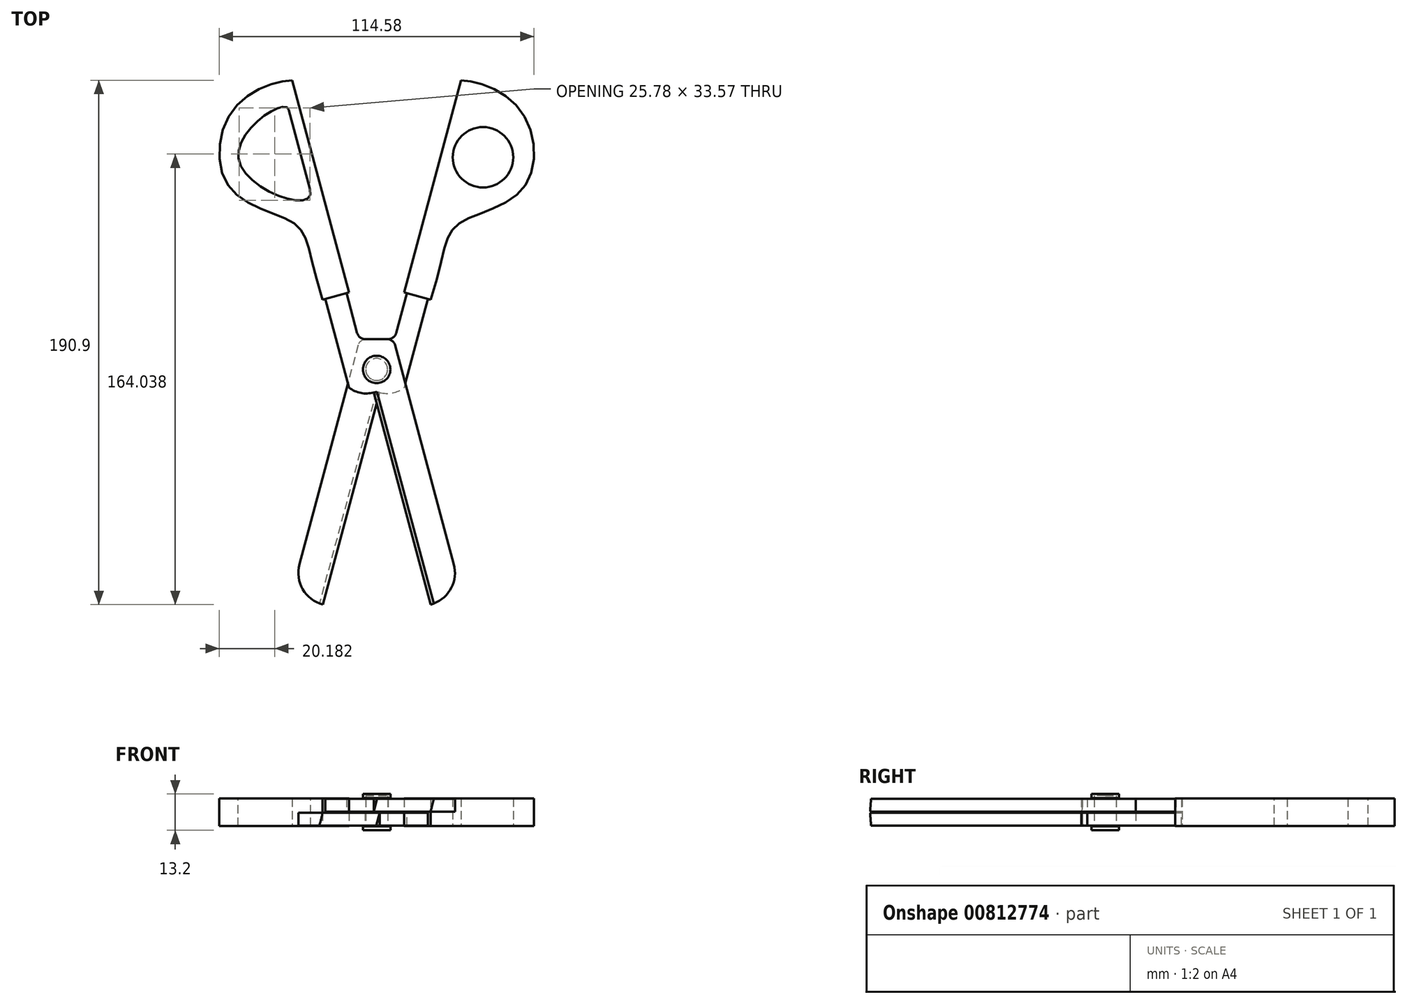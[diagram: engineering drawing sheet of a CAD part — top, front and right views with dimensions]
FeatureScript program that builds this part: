
annotation { "Feature Type Name" : "Feature", "Feature Type Description" : "" }
export const myFeature = defineFeature(function(context is Context, id is Id, definition is map)
    precondition{}
    {
        {
            var Q0;
            Q0=qCreatedBy(makeId("Top.planeOp"),FACE);
            var sketch = newSketch(context, id + "F0", { "sketchPlane" : qUnion([Q0])});
            skLineSegment(sketch, "E0", {"start": v(10, 10) * mm, "end": v(30.7, 87.27) * mm});
            skLineSegment(sketch, "E1", {"start": v(10, 10) * mm, "end": v(19.66, 7.41) * mm});
            skFitSpline(sketch, "E2", {"points": [v(19.66, 7.41) * mm, v(30.07, 35.15) * mm, v(53.27, 47.9) * mm, v(52.13, 76.77) * mm, v(30.7, 87.27) * mm], "startDerivative": vector(62.66, 194.88) * mm, "endDerivative": vector(-72.65, 2.28) * mm});
            skLineSegment(sketch, "E3.MirrorCS", {"start": v(-10, 10) * mm, "end": v(-30.7, 87.27) * mm});
            skFitSpline(sketch, "E4.MirrorCS", {"points": [v(-19.66, 7.41) * mm, v(-30.07, 35.15) * mm, v(-53.27, 47.9) * mm, v(-52.13, 76.77) * mm, v(-30.7, 87.27) * mm], "startDerivative": vector(-62.66, 194.88) * mm, "endDerivative": vector(72.65, 2.28) * mm});
            skLineSegment(sketch, "E5.MirrorCS", {"start": v(-10, 10) * mm, "end": v(-19.66, 7.41) * mm});
            skSolve(sketch);
        }
        {
            var Q0;
            Q0 = qSketchRegion(id + "F0", true);
            extrude(context, id + "F1", {"entities" : qUnion([Q0]), "endBound" : BoundingType.SYMMETRIC, "depth" : 10 * mm, "offsetDistance" : 25 * mm});
        }
        {
            var Q0;
            Q0=qCreatedBy(makeId("Top.planeOp"),FACE);
            var sketch = newSketch(context, id + "F2", { "sketchPlane" : qUnion([Q0])});
            skLineSegment(sketch, "E6", {"start": v(-31.98, 76.58) * mm, "end": v(-24.22, 47.6) * mm});
            skFitSpline(sketch, "E7", {"points": [v(-31.98, 76.58) * mm, v(-50.17, 58.1) * mm, v(-24.22, 47.6) * mm], "startDerivative": vector(-7.92, 29.54) * mm, "endDerivative": vector(-15.24, 56.87) * mm});
            skSolve(sketch);
        }
        {
            var Q0;
            Q0 = qSketchRegion(id + "F2", true);
            extrude(context, id + "F3", {"entities" : qUnion([Q0]), "operationType" : NewBodyOperationType.REMOVE, "endBound" : BoundingType.SYMMETRIC, "oppositeDirection" : true, "depth" : 40 * mm, "offsetDistance" : 25 * mm});
        }
        {
            var Q0;
            Q0=qCreatedBy(makeId("Top.planeOp"),FACE);
            var sketch = newSketch(context, id + "F4", { "sketchPlane" : qUnion([Q0])});
            skCircle(sketch, "E8", {"center": v(38.72, 59.24) * mm, "radius": 11 * mm});
            skSolve(sketch);
        }
        {
            var Q0;
            Q0 = qSketchRegion(id + "F4", true);
            extrude(context, id + "F5", {"entities" : qUnion([Q0]), "operationType" : NewBodyOperationType.REMOVE, "endBound" : BoundingType.SYMMETRIC, "depth" : 40 * mm, "offsetDistance" : 25 * mm});
        }
        {
            var Q0;
            Q0=qCreatedBy(makeId("Top.planeOp"),FACE);
            var sketch = newSketch(context, id + "F6", { "sketchPlane" : qUnion([Q0])});
            skCircle(sketch, "E9", {"center": v(0, -18) * mm, "radius": 4 * mm});
            skSolve(sketch);
        }
        {
            var Q0;
            Q0 = qSketchRegion(id + "F6", true);
            extrude(context, id + "F7", {"entities" : qUnion([Q0]), "endBound" : BoundingType.SYMMETRIC, "depth" : 12 * mm, "offsetDistance" : 25 * mm});
        }
        {
            var Q0;
            Q0=qCreatedBy(makeId("Top.planeOp"),FACE);
            cPlane(context, id + "F8", {"entities" : qUnion([Q0]), "cplaneType" : CPlaneType.OFFSET, "offset" : 2.5 * mm, "width" : 150 * mm, "height" : 150 * mm});
        }
        {
            var Q0;
            Q0=qCreatedBy(id+"F8.planeOp",FACE);
            var sketch = newSketch(context, id + "F9", { "sketchPlane" : qUnion([Q0])});
            skLineSegment(sketch, "E10", {"start": v(-19.99, 12.5) * mm, "end": v(-14.81, -6.82) * mm});
            skLineSegment(sketch, "E11", {"start": v(-12.26, 14.57) * mm, "end": v(-7.08, -4.75) * mm});
            skArc(sketch, "E12", {"start": v(-7.08, -4.75) * mm, "mid": v(-6.01, -6.35) * mm, "end": v(-4.19, -6.97) * mm});
            skLineSegment(sketch, "E13", {"start": v(-4.19, -6.97) * mm, "end": v(0, -6.97) * mm});
            skLineSegment(sketch, "E14.MirrorCS", {"start": v(4.19, -6.97) * mm, "end": v(0, -6.97) * mm});
            skArc(sketch, "E15", {"start": v(4.19, -6.97) * mm, "mid": v(5.8, -7.68) * mm, "end": v(6.73, -9.17) * mm});
            skLineSegment(sketch, "E16", {"start": v(6.73, -9.17) * mm, "end": v(28.1, -88.93) * mm});
            skLineSegment(sketch, "E17", {"start": v(-14.81, -6.82) * mm, "end": v(-10.04, -24.61) * mm});
            skArc(sketch, "E18", {"start": v(-10.04, -24.61) * mm, "mid": v(-5.78, -26.56) * mm, "end": v(-1.1, -26.35) * mm});
            skLineSegment(sketch, "E19", {"start": v(-1.1, -26.35) * mm, "end": v(19.61, -103.63) * mm});
            skArc(sketch, "E20", {"start": v(19.61, -103.63) * mm, "mid": v(26.9, -98.04) * mm, "end": v(28.1, -88.93) * mm});
            skLineSegment(sketch, "E21", {"start": v(-19.99, 12.5) * mm, "end": v(-12.26, 14.57) * mm});
            skSolve(sketch);
        }
        {
            var Q0;
            Q0 = qSketchRegion(id + "F9", true);
            extrude(context, id + "F10", {"entities" : qUnion([Q0]), "endBound" : BoundingType.SYMMETRIC, "depth" : 4.7 * mm, "offsetDistance" : 25 * mm});
        }
        {
            var Q0;
            Q0=qCreatedBy(makeId("Top.planeOp"),FACE);
            cPlane(context, id + "F11", {"entities" : qUnion([Q0]), "cplaneType" : CPlaneType.OFFSET, "offset" : 2.5 * mm, "oppositeDirection" : true, "width" : 150 * mm, "height" : 150 * mm});
        }
        {
            var Q0;
            Q0=qCreatedBy(id+"F11.planeOp",FACE);
            var sketch = newSketch(context, id + "F12", { "sketchPlane" : qUnion([Q0])});
            skLineSegment(sketch, "E22", {"start": v(12.26, 14.57) * mm, "end": v(7.08, -4.75) * mm});
            skLineSegment(sketch, "E23", {"start": v(19.99, 12.5) * mm, "end": v(14.81, -6.82) * mm});
            skArc(sketch, "E24", {"start": v(7.08, -4.75) * mm, "mid": v(6.01, -6.35) * mm, "end": v(4.19, -6.97) * mm});
            skLineSegment(sketch, "E25", {"start": v(4.19, -6.97) * mm, "end": v(0, -6.97) * mm});
            skLineSegment(sketch, "E26.MirrorCS", {"start": v(-4.19, -6.97) * mm, "end": v(0, -6.97) * mm});
            skArc(sketch, "E27", {"start": v(-4.19, -6.97) * mm, "mid": v(-5.8, -7.68) * mm, "end": v(-6.73, -9.17) * mm});
            skLineSegment(sketch, "E28", {"start": v(-6.73, -9.17) * mm, "end": v(-28.1, -88.93) * mm});
            skLineSegment(sketch, "E29", {"start": v(14.81, -6.82) * mm, "end": v(10.04, -24.61) * mm});
            skArc(sketch, "E30", {"start": v(10.04, -24.61) * mm, "mid": v(5.78, -26.56) * mm, "end": v(1.1, -26.35) * mm});
            skLineSegment(sketch, "E31", {"start": v(1.1, -26.35) * mm, "end": v(-19.61, -103.63) * mm});
            skArc(sketch, "E32", {"start": v(-28.1, -88.93) * mm, "mid": v(-26.9, -98.04) * mm, "end": v(-19.61, -103.63) * mm});
            skLineSegment(sketch, "E33", {"start": v(12.26, 14.57) * mm, "end": v(19.99, 12.5) * mm});
            skSolve(sketch);
        }
        {
            var Q0;
            Q0=makeQuery(id+"F10.opExtrude","SWEPT_FACE",FACE,{"disambiguationData":[OSD([sQuery(id+"F9.wireOp",EDGE,"E21")])]});
            cPlane(context, id + "F13", {"entities" : qUnion([Q0]), "cplaneType" : CPlaneType.OFFSET, "offset" : 122.5 * mm, "oppositeDirection" : true, "width" : 150 * mm, "height" : 150 * mm});
        }
        {
            var Q0;
            Q0=qCreatedBy(id+"F13.planeOp",FACE);
            var sketch = newSketch(context, id + "F14", { "sketchPlane" : qUnion([Q0])});
            skLineSegment(sketch, "E34", {"start": v(7.88, 0.15) * mm, "end": v(6.62, 4.85) * mm});
            skLineSegment(sketch, "E35", {"start": v(6.62, 4.85) * mm, "end": v(7.88, 4.85) * mm});
            skLineSegment(sketch, "E36", {"start": v(7.88, 4.85) * mm, "end": v(7.88, 0.15) * mm});
            skSolve(sketch);
        }
        {
            var Q0;
            Q0 = qSketchRegion(id + "F14", true);
            extrude(context, id + "F15", {"entities" : qUnion([Q0]), "operationType" : NewBodyOperationType.REMOVE, "depth" : 80 * mm, "offsetDistance" : 25 * mm});
        }
        {
            var Q0;
            Q0 = qSketchRegion(id + "F12", true);
            extrude(context, id + "F16", {"entities" : qUnion([Q0]), "endBound" : BoundingType.SYMMETRIC, "depth" : 4.7 * mm, "offsetDistance" : 25 * mm});
        }
        {
            var Q0;
            Q0=makeQuery(id+"F10.opExtrude","CAP_FACE",FACE,{"disambiguationData":[OSD([sQuery(id+"F9.wireOp",EDGE,"E10"),sQuery(id+"F9.wireOp",EDGE,"E11"),sQuery(id+"F9.wireOp",EDGE,"E12"),sQuery(id+"F9.wireOp",EDGE,"E13"),sQuery(id+"F9.wireOp",EDGE,"E14.MirrorCS"),sQuery(id+"F9.wireOp",EDGE,"E15"),sQuery(id+"F9.wireOp",EDGE,"E16"),sQuery(id+"F9.wireOp",EDGE,"E17"),sQuery(id+"F9.wireOp",EDGE,"E18"),sQuery(id+"F9.wireOp",EDGE,"E19"),sQuery(id+"F9.wireOp",EDGE,"E20"),sQuery(id+"F9.wireOp",EDGE,"E21")])],"isStart":false});
            cPlane(context, id + "F17", {"entities" : qUnion([Q0]), "cplaneType" : CPlaneType.OFFSET, "offset" : 1 * mm, "width" : 150 * mm, "height" : 150 * mm});
        }
        {
            var Q0;
            Q0=qCreatedBy(id+"F17.planeOp",FACE);
            var sketch = newSketch(context, id + "F18", { "sketchPlane" : qUnion([Q0])});
            skCircle(sketch, "E37", {"center": v(0, -18) * mm, "radius": 5 * mm});
            skSolve(sketch);
        }
        {
            var Q0;
            Q0 = qSketchRegion(id + "F18", true);
            extrude(context, id + "F19", {"entities" : qUnion([Q0]), "endBound" : BoundingType.SYMMETRIC, "depth" : 1.5 * mm, "offsetDistance" : 25 * mm});
        }
        {
            var Q0;
            Q0=makeQuery(id+"F16.opExtrude","SWEPT_FACE",FACE,{"disambiguationData":[OSD([sQuery(id+"F12.wireOp",EDGE,"E33")])]});
            cPlane(context, id + "F20", {"entities" : qUnion([Q0]), "cplaneType" : CPlaneType.OFFSET, "offset" : 122.5 * mm, "oppositeDirection" : true, "width" : 150 * mm, "height" : 150 * mm});
        }
        {
            var Q0;
            Q0=qCreatedBy(id+"F20.planeOp",FACE);
            var sketch = newSketch(context, id + "F21", { "sketchPlane" : qUnion([Q0])});
            skLineSegment(sketch, "E38", {"start": v(-7.88, -0.15) * mm, "end": v(-7.88, -4.85) * mm});
            skLineSegment(sketch, "E39", {"start": v(-7.88, -4.85) * mm, "end": v(-6.62, -4.85) * mm});
            skLineSegment(sketch, "E40", {"start": v(-6.62, -4.85) * mm, "end": v(-7.88, -0.15) * mm});
            skSolve(sketch);
        }
        {
            var Q0;
            Q0 = qSketchRegion(id + "F21", true);
            extrude(context, id + "F22", {"entities" : qUnion([Q0]), "operationType" : NewBodyOperationType.REMOVE, "depth" : 80 * mm, "offsetDistance" : 25 * mm});
        }
        {
            var Q0;
            Q0=makeQuery(id+"F16.opExtrude","CAP_FACE",FACE,{"disambiguationData":[OSD([sQuery(id+"F12.wireOp",EDGE,"E22"),sQuery(id+"F12.wireOp",EDGE,"E23"),sQuery(id+"F12.wireOp",EDGE,"E24"),sQuery(id+"F12.wireOp",EDGE,"E25"),sQuery(id+"F12.wireOp",EDGE,"E26.MirrorCS"),sQuery(id+"F12.wireOp",EDGE,"E27"),sQuery(id+"F12.wireOp",EDGE,"E28"),sQuery(id+"F12.wireOp",EDGE,"E29"),sQuery(id+"F12.wireOp",EDGE,"E30"),sQuery(id+"F12.wireOp",EDGE,"E31"),sQuery(id+"F12.wireOp",EDGE,"E32"),sQuery(id+"F12.wireOp",EDGE,"E33")])],"isStart":true});
            cPlane(context, id + "F23", {"entities" : qUnion([Q0]), "cplaneType" : CPlaneType.OFFSET, "offset" : 1 * mm, "width" : 150 * mm, "height" : 150 * mm});
        }
        {
            var Q0;
            Q0=qCreatedBy(id+"F23.planeOp",FACE);
            var sketch = newSketch(context, id + "F24", { "sketchPlane" : qUnion([Q0])});
            skCircle(sketch, "E41", {"center": v(0, 18) * mm, "radius": 5 * mm});
            skSolve(sketch);
        }
        {
            var Q0;
            Q0 = qSketchRegion(id + "F24", true);
            extrude(context, id + "F25", {"entities" : qUnion([Q0]), "operationType" : NewBodyOperationType.ADD, "endBound" : BoundingType.SYMMETRIC, "depth" : 1.5 * mm, "offsetDistance" : 25 * mm});
        }
        {
            var Q0;
            Q0=makeQuery(id+"F1.opExtrude","SWEPT_BODY",BODY,{"disambiguationData":[OSD([sQuery(id+"F0.wireOp",EDGE,"E0"),sQuery(id+"F0.wireOp",EDGE,"E1"),sQuery(id+"F0.wireOp",EDGE,"E2")])]});
            var Q1;
            Q1=makeQuery(id+"F16.opExtrude","SWEPT_BODY",BODY,{"disambiguationData":[OSD([sQuery(id+"F12.wireOp",EDGE,"E22"),sQuery(id+"F12.wireOp",EDGE,"E23"),sQuery(id+"F12.wireOp",EDGE,"E24"),sQuery(id+"F12.wireOp",EDGE,"E25"),sQuery(id+"F12.wireOp",EDGE,"E26.MirrorCS"),sQuery(id+"F12.wireOp",EDGE,"E27"),sQuery(id+"F12.wireOp",EDGE,"E28"),sQuery(id+"F12.wireOp",EDGE,"E29"),sQuery(id+"F12.wireOp",EDGE,"E30"),sQuery(id+"F12.wireOp",EDGE,"E31"),sQuery(id+"F12.wireOp",EDGE,"E32"),sQuery(id+"F12.wireOp",EDGE,"E33")])]});
            booleanBodies(context, id + "F26", {"operationType" : BooleanOperationType.SUBTRACTION, "tools" : qUnion([Q0]), "targets" : qUnion([Q1]), "keepTools" : true});
        }
        {
            var Q0;
            Q0=makeQuery(id+"F1.opExtrude","SWEPT_BODY",BODY,{"disambiguationData":[OSD([sQuery(id+"F0.wireOp",EDGE,"E3.MirrorCS"),sQuery(id+"F0.wireOp",EDGE,"E4.MirrorCS"),sQuery(id+"F0.wireOp",EDGE,"E5.MirrorCS")])]});
            var Q1;
            Q1=makeQuery(id+"F10.opExtrude","SWEPT_BODY",BODY,{"disambiguationData":[OSD([sQuery(id+"F9.wireOp",EDGE,"E10"),sQuery(id+"F9.wireOp",EDGE,"E11"),sQuery(id+"F9.wireOp",EDGE,"E12"),sQuery(id+"F9.wireOp",EDGE,"E13"),sQuery(id+"F9.wireOp",EDGE,"E14.MirrorCS"),sQuery(id+"F9.wireOp",EDGE,"E15"),sQuery(id+"F9.wireOp",EDGE,"E16"),sQuery(id+"F9.wireOp",EDGE,"E17"),sQuery(id+"F9.wireOp",EDGE,"E18"),sQuery(id+"F9.wireOp",EDGE,"E19"),sQuery(id+"F9.wireOp",EDGE,"E20"),sQuery(id+"F9.wireOp",EDGE,"E21")])]});
            booleanBodies(context, id + "F27", {"operationType" : BooleanOperationType.SUBTRACTION, "tools" : qUnion([Q0]), "targets" : qUnion([Q1]), "keepTools" : true});
        }
        {
            var Q0;
            Q0=makeQuery(id+"F7.opExtrude","SWEPT_BODY",BODY,{"disambiguationData":[OSD([sQuery(id+"F6.wireOp",EDGE,"E9")])]});
            var Q1;
            Q1=makeQuery(id+"F16.opExtrude","SWEPT_BODY",BODY,{"disambiguationData":[OSD([sQuery(id+"F12.wireOp",EDGE,"E22"),sQuery(id+"F12.wireOp",EDGE,"E23"),sQuery(id+"F12.wireOp",EDGE,"E24"),sQuery(id+"F12.wireOp",EDGE,"E25"),sQuery(id+"F12.wireOp",EDGE,"E26.MirrorCS"),sQuery(id+"F12.wireOp",EDGE,"E27"),sQuery(id+"F12.wireOp",EDGE,"E28"),sQuery(id+"F12.wireOp",EDGE,"E29"),sQuery(id+"F12.wireOp",EDGE,"E30"),sQuery(id+"F12.wireOp",EDGE,"E31"),sQuery(id+"F12.wireOp",EDGE,"E32"),sQuery(id+"F12.wireOp",EDGE,"E33")])]});
            var Q2;
            Q2=makeQuery(id+"F10.opExtrude","SWEPT_BODY",BODY,{"disambiguationData":[OSD([sQuery(id+"F9.wireOp",EDGE,"E10"),sQuery(id+"F9.wireOp",EDGE,"E11"),sQuery(id+"F9.wireOp",EDGE,"E12"),sQuery(id+"F9.wireOp",EDGE,"E13"),sQuery(id+"F9.wireOp",EDGE,"E14.MirrorCS"),sQuery(id+"F9.wireOp",EDGE,"E15"),sQuery(id+"F9.wireOp",EDGE,"E16"),sQuery(id+"F9.wireOp",EDGE,"E17"),sQuery(id+"F9.wireOp",EDGE,"E18"),sQuery(id+"F9.wireOp",EDGE,"E19"),sQuery(id+"F9.wireOp",EDGE,"E20"),sQuery(id+"F9.wireOp",EDGE,"E21")])]});
            booleanBodies(context, id + "F28", {"operationType" : BooleanOperationType.SUBTRACTION, "tools" : qUnion([Q0]), "targets" : qUnion([Q1, Q2]), "keepTools" : true});
        }
    });
